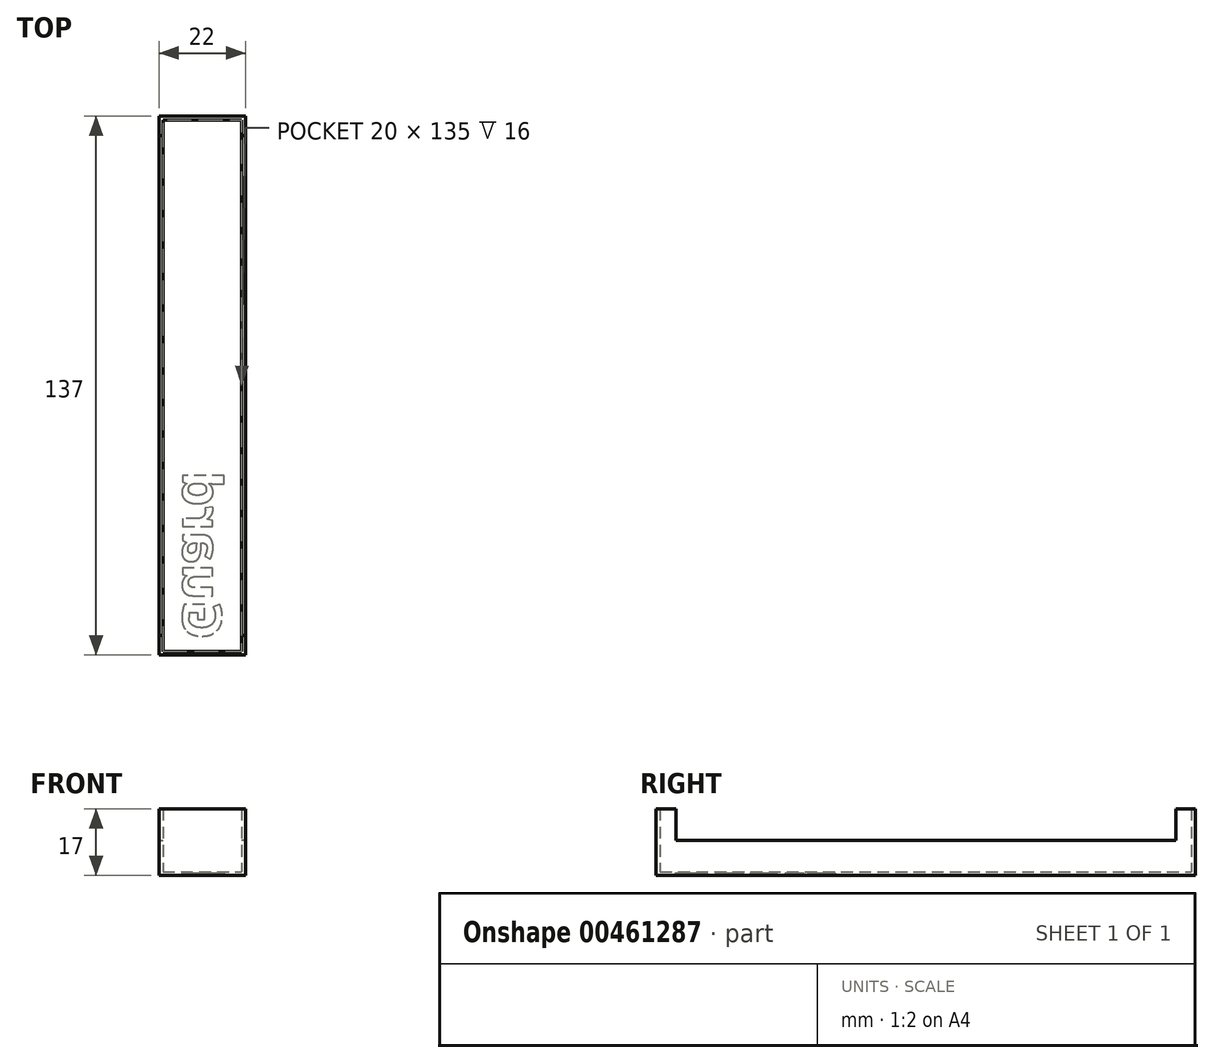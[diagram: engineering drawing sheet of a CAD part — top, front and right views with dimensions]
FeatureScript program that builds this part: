
annotation { "Feature Type Name" : "Feature", "Feature Type Description" : "" }
export const myFeature = defineFeature(function(context is Context, id is Id, definition is map)
    precondition{}
    {
        {
            var Q0;
            Q0=qCreatedBy(makeId("Top.planeOp"),FACE);
            var sketch = newSketch(context, id + "F0", { "sketchPlane" : qUnion([Q0])});
            skLineSegment(sketch, "E0.bottom", {"start": v(-11, 68.5) * mm, "end": v(11, 68.5) * mm});
            skLineSegment(sketch, "E0.top", {"start": v(-11, -68.5) * mm, "end": v(11, -68.5) * mm});
            skLineSegment(sketch, "E0.left", {"start": v(-11, 68.5) * mm, "end": v(-11, -68.5) * mm});
            skLineSegment(sketch, "E0.right", {"start": v(11, 68.5) * mm, "end": v(11, -68.5) * mm});
            skPoint(sketch, "E0.middle", {"position": v(0, 0) * mm});
            skSolve(sketch);
        }
        {
            var Q0;
            Q0 = qSketchRegion(id + "F0", true);
            extrude(context, id + "F1", {"entities" : qUnion([Q0]), "depth" : 1 * mm});
        }
        {
            var Q0;
            Q0=makeQuery(id+"F1.opExtrude","CAP_FACE",FACE,{"disambiguationData":[OSD([sQuery(id+"F0.wireOp",EDGE,"E0.bottom"),sQuery(id+"F0.wireOp",EDGE,"E0.top"),sQuery(id+"F0.wireOp",EDGE,"E0.left"),sQuery(id+"F0.wireOp",EDGE,"E0.right")])],"isStart":false});
            var sketch = newSketch(context, id + "F2", { "sketchPlane" : qUnion([Q0])});
            skLineSegment(sketch, "E1.bottom", {"start": v(-11, 68.5) * mm, "end": v(11, 68.5) * mm});
            skLineSegment(sketch, "E1.top", {"start": v(-11, 67.5) * mm, "end": v(11, 67.5) * mm});
            skLineSegment(sketch, "E1.left", {"start": v(-11, 68.5) * mm, "end": v(-11, 67.5) * mm});
            skLineSegment(sketch, "E1.right", {"start": v(11, 68.5) * mm, "end": v(11, 67.5) * mm});
            skLineSegment(sketch, "E2.bottom", {"start": v(-11, 63.5) * mm, "end": v(-10, 63.5) * mm});
            skLineSegment(sketch, "E2.top", {"start": v(-11, 67.5) * mm, "end": v(-10, 67.5) * mm});
            skLineSegment(sketch, "E2.left", {"start": v(-11, 63.5) * mm, "end": v(-11, 67.5) * mm});
            skLineSegment(sketch, "E2.right", {"start": v(-10, 63.5) * mm, "end": v(-10, 67.5) * mm});
            skLineSegment(sketch, "E3.bottom", {"start": v(11, 63.5) * mm, "end": v(10, 63.5) * mm});
            skLineSegment(sketch, "E3.top", {"start": v(11, 67.5) * mm, "end": v(10, 67.5) * mm});
            skLineSegment(sketch, "E3.left", {"start": v(11, 63.5) * mm, "end": v(11, 67.5) * mm});
            skLineSegment(sketch, "E3.right", {"start": v(10, 63.5) * mm, "end": v(10, 67.5) * mm});
            skLineSegment(sketch, "E4.bottom", {"start": v(-11, -68.5) * mm, "end": v(11, -68.5) * mm});
            skLineSegment(sketch, "E4.top", {"start": v(-11, -67.5) * mm, "end": v(11, -67.5) * mm});
            skLineSegment(sketch, "E4.left", {"start": v(-11, -68.5) * mm, "end": v(-11, -67.5) * mm});
            skLineSegment(sketch, "E4.right", {"start": v(11, -68.5) * mm, "end": v(11, -67.5) * mm});
            skLineSegment(sketch, "E5.bottom", {"start": v(-11, -63.5) * mm, "end": v(-10, -63.5) * mm});
            skLineSegment(sketch, "E5.top", {"start": v(-11, -67.5) * mm, "end": v(-10, -67.5) * mm});
            skLineSegment(sketch, "E5.left", {"start": v(-11, -63.5) * mm, "end": v(-11, -67.5) * mm});
            skLineSegment(sketch, "E5.right", {"start": v(-10, -63.5) * mm, "end": v(-10, -67.5) * mm});
            skLineSegment(sketch, "E6.bottom", {"start": v(11, -63.5) * mm, "end": v(10, -63.5) * mm});
            skLineSegment(sketch, "E6.top", {"start": v(11, -67.5) * mm, "end": v(10, -67.5) * mm});
            skLineSegment(sketch, "E6.left", {"start": v(11, -63.5) * mm, "end": v(11, -67.5) * mm});
            skLineSegment(sketch, "E6.right", {"start": v(10, -63.5) * mm, "end": v(10, -67.5) * mm});
            skSolve(sketch);
        }
        {
            var Q0;
            Q0 = qSketchRegion(id + "F2", true);
            extrude(context, id + "F3", {"entities" : qUnion([Q0]), "operationType" : NewBodyOperationType.ADD, "depth" : 16 * mm});
        }
        {
            var Q0;
            Q0=makeQuery(id+"F1.opExtrude","CAP_FACE",FACE,{"disambiguationData":[OSD([sQuery(id+"F0.wireOp",EDGE,"E0.bottom"),sQuery(id+"F0.wireOp",EDGE,"E0.top"),sQuery(id+"F0.wireOp",EDGE,"E0.left"),sQuery(id+"F0.wireOp",EDGE,"E0.right")])],"isStart":false});
            var sketch = newSketch(context, id + "F4", { "sketchPlane" : qUnion([Q0])});
            skLineSegment(sketch, "E7.bottom", {"start": v(10, 63.5) * mm, "end": v(11, 63.5) * mm});
            skLineSegment(sketch, "E7.top", {"start": v(10, -63.5) * mm, "end": v(11, -63.5) * mm});
            skLineSegment(sketch, "E7.left", {"start": v(10, 63.5) * mm, "end": v(10, -63.5) * mm});
            skLineSegment(sketch, "E7.right", {"start": v(11, 63.5) * mm, "end": v(11, -63.5) * mm});
            skLineSegment(sketch, "E8.bottom", {"start": v(-11, 63.5) * mm, "end": v(-10, 63.5) * mm});
            skLineSegment(sketch, "E8.top", {"start": v(-11, -63.5) * mm, "end": v(-10, -63.5) * mm});
            skLineSegment(sketch, "E8.left", {"start": v(-11, 63.5) * mm, "end": v(-11, -63.5) * mm});
            skLineSegment(sketch, "E8.right", {"start": v(-10, 63.5) * mm, "end": v(-10, -63.5) * mm});
            skSolve(sketch);
        }
        {
            var Q0;
            Q0 = qSketchRegion(id + "F4", true);
            extrude(context, id + "F5", {"entities" : qUnion([Q0]), "operationType" : NewBodyOperationType.ADD, "depth" : 8 * mm});
        }
        {
            var Q0;
            Q0=makeQuery(id+"F1.opExtrude","CAP_FACE",FACE,{"disambiguationData":[OSD([sQuery(id+"F0.wireOp",EDGE,"E0.bottom"),sQuery(id+"F0.wireOp",EDGE,"E0.top"),sQuery(id+"F0.wireOp",EDGE,"E0.left"),sQuery(id+"F0.wireOp",EDGE,"E0.right")])],"isStart":true});
            var sketch = newSketch(context, id + "F6", { "sketchPlane" : qUnion([Q0])});
            skText(sketch, "E9", { "text": "Guard", "fontName": "OpenSans-Bold.ttf"});
            const initialGuessF6  = {"E9": [-0.005, 0.0645, 0, -1, 0.01]};
            skSetInitialGuess(sketch, initialGuessF6);
            skSolve(sketch);
        }
        {
            var Q0;
            Q0 = qSketchRegion(id + "F6", true);
            extrude(context, id + "F7", {"entities" : qUnion([Q0]), "operationType" : NewBodyOperationType.REMOVE, "oppositeDirection" : true, "depth" : 0.5 * mm});
        }
    });
